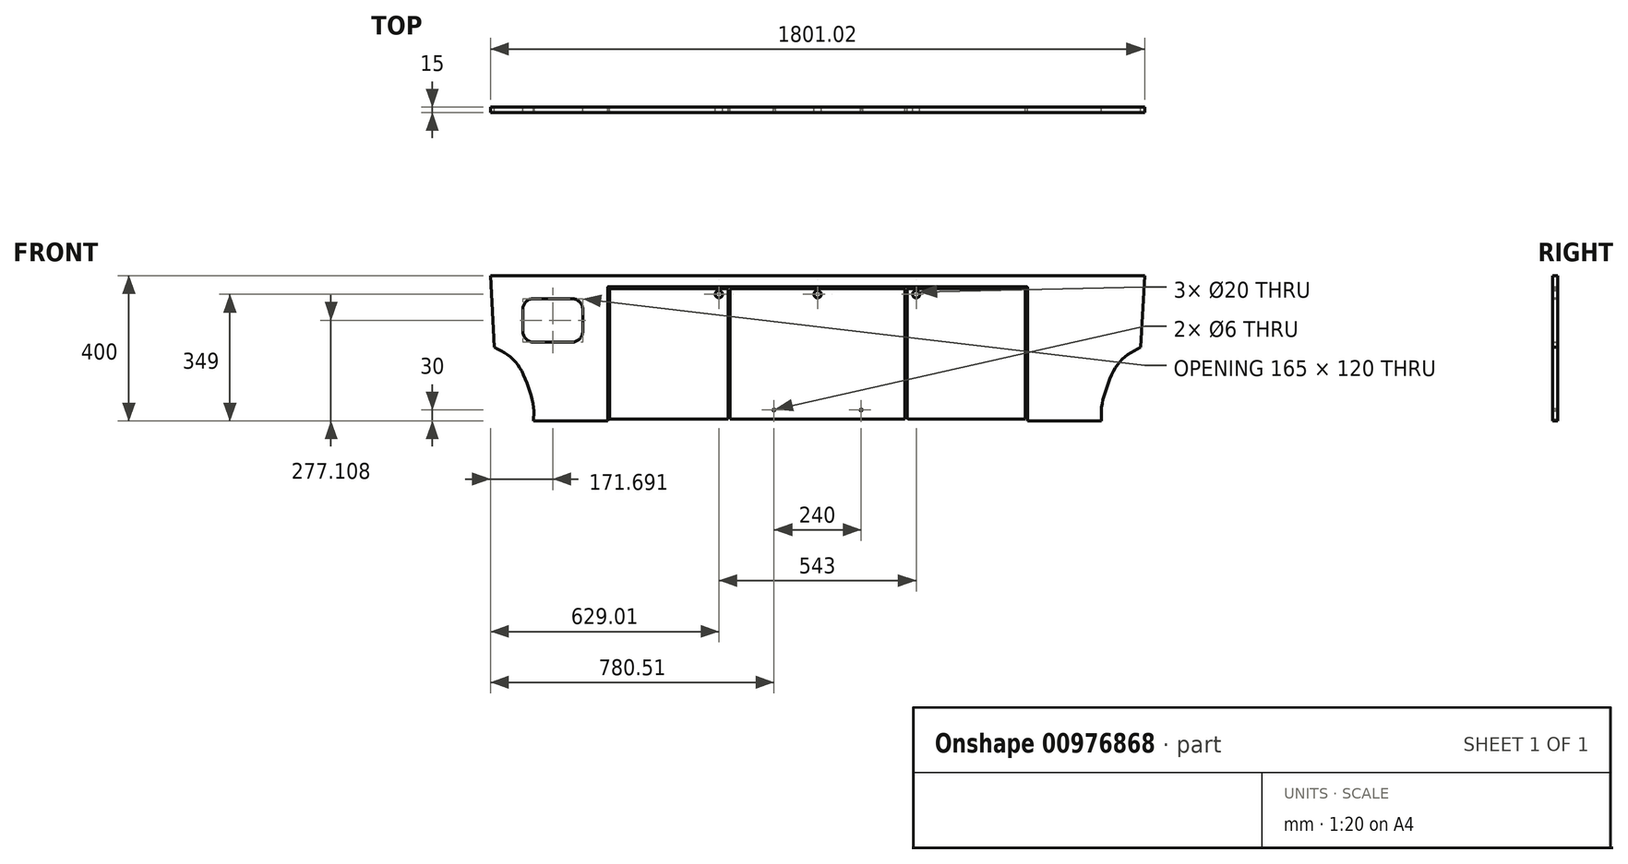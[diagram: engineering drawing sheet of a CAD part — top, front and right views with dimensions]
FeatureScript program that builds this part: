
annotation { "Feature Type Name" : "Feature", "Feature Type Description" : "" }
export const myFeature = defineFeature(function(context is Context, id is Id, definition is map)
    precondition{}
    {
        {
            var Q0;
            Q0=qCreatedBy(makeId("Front.planeOp"),FACE);
            var sketch = newSketch(context, id + "F0", { "sketchPlane" : qUnion([Q0])});
            skLineSegment(sketch, "E0", {"start": v(0, 0) * mm, "end": v(3, 0) * mm});
            skLineSegment(sketch, "E1", {"start": v(575, 0) * mm, "end": v(575, 400) * mm, "construction": true});
            skLineSegment(sketch, "E2", {"start": v(1150, 0) * mm, "end": v(1150, 367) * mm, "construction": true});
            skPoint(sketch, "E3", {"position": v(1357, 0) * mm});
            skLineSegment(sketch, "E4", {"start": v(1153, 0) * mm, "end": v(1357, 0) * mm});
            skPoint(sketch, "E5", {"position": v(1357, 38.33) * mm});
            skPoint(sketch, "E6", {"position": v(1371.58, 94.24) * mm});
            skPoint(sketch, "E7", {"position": v(1395.53, 147.48) * mm});
            skPoint(sketch, "E8", {"position": v(1424.82, 179.42) * mm});
            skPoint(sketch, "E9", {"position": v(1464.75, 203.38) * mm});
            skLineSegment(sketch, "E10.MirrorCS", {"start": v(0, 0) * mm, "end": v(-207, 0) * mm});
            skFitSpline(sketch, "E11", {"points": [v(1357, 0) * mm, v(1357, 38.33) * mm, v(1371.58, 94.24) * mm, v(1395.53, 147.48) * mm, v(1424.82, 179.42) * mm, v(1464.75, 203.38) * mm], "startDerivative": vector(-14.06, 206.16) * mm, "endDerivative": vector(214.46, 114.18) * mm});
            skLineSegment(sketch, "E12", {"start": v(575, 400) * mm, "end": v(1475.51, 400) * mm});
            skLineSegment(sketch, "E13", {"start": v(1475.51, 400) * mm, "end": v(1464.75, 203.38) * mm});
            skLineSegment(sketch, "E14.MirrorCS", {"start": v(575, 400) * mm, "end": v(-325.51, 400) * mm});
            skLineSegment(sketch, "E15.MirrorCS", {"start": v(-325.51, 400) * mm, "end": v(-314.75, 203.38) * mm});
            skFitSpline(sketch, "E16.MirrorCS", {"points": [v(-207, 0) * mm, v(-207, 38.33) * mm, v(-221.58, 94.24) * mm, v(-245.53, 147.48) * mm, v(-274.82, 179.42) * mm, v(-314.75, 203.38) * mm], "startDerivative": vector(14.06, 206.16) * mm, "endDerivative": vector(-214.46, 114.18) * mm});
            skLineSegment(sketch, "E17", {"start": v(0, 367) * mm, "end": v(1150, 367) * mm, "construction": true});
            skLineSegment(sketch, "E18", {"start": v(0, 367) * mm, "end": v(0, 0) * mm, "construction": true});
            skArc(sketch, "E19.0.startCap", {"start": v(-3, 367) * mm, "mid": v(-2.12, 369.12) * mm, "end": v(0, 370) * mm});
            skArc(sketch, "E19.0.endCap", {"start": v(1150, 370) * mm, "mid": v(1152.12, 369.12) * mm, "end": v(1153, 367) * mm});
            skLineSegment(sketch, "E19.0.left", {"start": v(0, 370) * mm, "end": v(1150, 370) * mm});
            skLineSegment(sketch, "E19.0.right", {"start": v(3, 364) * mm, "end": v(323.5, 364) * mm});
            skLineSegment(sketch, "E20.0.left", {"start": v(3, 364) * mm, "end": v(3, 5) * mm});
            skLineSegment(sketch, "E20.0.right", {"start": v(-3, 367) * mm, "end": v(-3, 0) * mm});
            skLineSegment(sketch, "E21.MirrorCS", {"start": v(331.5, 0) * mm, "end": v(331.5, 367) * mm, "construction": true});
            skLineSegment(sketch, "E22.0.left", {"start": v(328.5, 5) * mm, "end": v(328.5, 359) * mm});
            skLineSegment(sketch, "E22.0.right", {"start": v(334.5, 5) * mm, "end": v(334.5, 359) * mm});
            skLineSegment(sketch, "E23.trimOffspring", {"start": v(339.5, 364) * mm, "end": v(810.5, 364) * mm});
            skLineSegment(sketch, "E24.MirrorCS", {"start": v(821.5, 5) * mm, "end": v(821.5, 364) * mm});
            skLineSegment(sketch, "E25.MirrorCS", {"start": v(1147, 364) * mm, "end": v(821.5, 364) * mm});
            skLineSegment(sketch, "E26.MirrorCS", {"start": v(1147, 364) * mm, "end": v(1147, 5) * mm});
            skLineSegment(sketch, "E27.MirrorCS", {"start": v(818.5, 0) * mm, "end": v(818.5, 367) * mm, "construction": true});
            skLineSegment(sketch, "E28.MirrorCS", {"start": v(815.5, 5) * mm, "end": v(815.5, 359) * mm});
            skLineSegment(sketch, "E29.MirrorCS", {"start": v(1153, 367) * mm, "end": v(1153, 0) * mm});
            skLineSegment(sketch, "E30.trimOffspring", {"start": v(821.5, 364) * mm, "end": v(1147, 364) * mm});
            skPoint(sketch, "E20.1.startCap.center.orphan", {"position": v(818.5, 0) * mm});
            skLineSegment(sketch, "E31.bottom", {"start": v(-101.32, 337.1) * mm, "end": v(-206.32, 337.1) * mm});
            skLineSegment(sketch, "E31.top", {"start": v(-101.32, 217.1) * mm, "end": v(-206.32, 217.1) * mm});
            skLineSegment(sketch, "E31.left", {"start": v(-71.32, 307.1) * mm, "end": v(-71.32, 247.1) * mm});
            skLineSegment(sketch, "E31.right", {"start": v(-236.32, 307.1) * mm, "end": v(-236.32, 247.1) * mm});
            skPoint(sketch, "E31.middle", {"position": v(-153.82, 277.1) * mm});
            skPoint(sketch, "E32.visualSharp", {"position": v(-71.32, 337.1) * mm});
            skArc(sketch, "E32.filletArc", {"start": v(-71.32, 307.1) * mm, "mid": v(-80.1, 328.32) * mm, "end": v(-101.32, 337.1) * mm});
            skPoint(sketch, "E33.visualSharp", {"position": v(-236.32, 337.1) * mm});
            skArc(sketch, "E33.filletArc", {"start": v(-206.32, 337.1) * mm, "mid": v(-227.53, 328.32) * mm, "end": v(-236.32, 307.1) * mm});
            skPoint(sketch, "E34.visualSharp", {"position": v(-71.32, 217.1) * mm});
            skArc(sketch, "E34.filletArc", {"start": v(-101.32, 217.1) * mm, "mid": v(-80.1, 225.9) * mm, "end": v(-71.32, 247.1) * mm});
            skPoint(sketch, "E35.visualSharp", {"position": v(-236.32, 217.1) * mm});
            skArc(sketch, "E35.filletArc", {"start": v(-236.32, 247.1) * mm, "mid": v(-227.53, 225.9) * mm, "end": v(-206.32, 217.1) * mm});
            skPoint(sketch, "E36.MirrorP", {"position": v(392.64, 490.65) * mm});
            skPoint(sketch, "E37", {"position": v(1147, 5) * mm});
            skPoint(sketch, "E38.MirrorP", {"position": v(3, 5) * mm});
            skLineSegment(sketch, "E39", {"start": v(1147, 5) * mm, "end": v(3, 5) * mm});
            skPoint(sketch, "E40.orphan", {"position": v(3, 0) * mm});
            skPoint(sketch, "E41.orphan", {"position": v(334.5, 0) * mm});
            skPoint(sketch, "E42.orphan", {"position": v(328.5, 0) * mm});
            skPoint(sketch, "E43.orphan", {"position": v(815.5, 0) * mm});
            skPoint(sketch, "E44.orphan", {"position": v(821.5, 0) * mm});
            skPoint(sketch, "E45.trimOffspring.start.orphan", {"position": v(1147, 0) * mm});
            skPoint(sketch, "E46.visualSharp", {"position": v(328.5, 364) * mm});
            skArc(sketch, "E46.filletArc", {"start": v(328.5, 359) * mm, "mid": v(327.04, 362.54) * mm, "end": v(323.5, 364) * mm});
            skPoint(sketch, "E47.visualSharp", {"position": v(334.5, 364) * mm});
            skArc(sketch, "E47.filletArc", {"start": v(339.5, 364) * mm, "mid": v(335.96, 362.54) * mm, "end": v(334.5, 359) * mm});
            skPoint(sketch, "E48.visualSharp", {"position": v(815.5, 364) * mm});
            skArc(sketch, "E48.filletArc", {"start": v(815.5, 359) * mm, "mid": v(814.04, 362.54) * mm, "end": v(810.5, 364) * mm});
            skSolve(sketch);
        }
        {
            var Q0;
            {var subQ3=sQuery(id+"F0.wireOp",EDGE,"E20.0.endCap");Q0=makeQuery(id+"F0.imprint","IMPRINT",FACE,{"disambiguationData":[TD([[makeQuery(id+"F0.imprint","IMPRINT",EDGE,{"derivedFrom":subQ3}),-1.0]])]});}
            var Q1;
            {var subQ0=sQuery(id+"F0.wireOp",EDGE,"E20.1.startCap");Q1=makeQuery(id+"F0.imprint","IMPRINT",FACE,{"disambiguationData":[TD([[makeQuery(id+"F0.imprint","IMPRINT",EDGE,{"derivedFrom":subQ0}),-1.0]])]});}
            var Q2;
            {var subQ0=sQuery(id+"F0.wireOp",EDGE,"E20.0.left");var subQ5=sQuery(id+"F0.wireOp",EDGE,"E19.0.right");var subQ6=makeQuery(id+"F0.imprint","INTERSECT",VERTEX,{"derivedFrom":[subQ5,subQ0]});Q2=makeQuery(id+"F0.imprint","IMPRINT",FACE,{"disambiguationData":[TD([[makeQuery(id+"F0.imprint","IMPRINT",EDGE,{"disambiguationData":[TD([[subQ6,-1.0]])],"derivedFrom":subQ5}),-1.0]])]});}
            var Q3;
            {var subQ1=sQuery(id+"F0.wireOp",EDGE,"E19.0.startCap");Q3=makeQuery(id+"F0.imprint","IMPRINT",FACE,{"disambiguationData":[TD([[makeQuery(id+"F0.imprint","IMPRINT",EDGE,{"derivedFrom":subQ1}),1.0]])]});}
            var Q4;
            {var subQ4=sQuery(id+"F0.wireOp",EDGE,"E20.1.left");var subQ6=sQuery(id+"F0.wireOp",EDGE,"E19.0.right");var subQ7=makeQuery(id+"F0.imprint","INTERSECT",VERTEX,{"derivedFrom":[subQ6,subQ4]});Q4=makeQuery(id+"F0.imprint","IMPRINT",FACE,{"disambiguationData":[TD([[makeQuery(id+"F0.imprint","IMPRINT",EDGE,{"disambiguationData":[TD([[subQ7,-1.0]])],"derivedFrom":subQ6}),-1.0]])]});}
            var Q5;
            {var subQ0=sQuery(id+"F0.wireOp",EDGE,"E26.MirrorCS");Q5=makeQuery(id+"F0.imprint","IMPRINT",FACE,{"disambiguationData":[TD([[makeQuery(id+"F0.imprint","IMPRINT",EDGE,{"derivedFrom":subQ0}),-1.0]])]});}
            var Q6;
            {var subQ1=sQuery(id+"F0.wireOp",EDGE,"E11");Q6=makeQuery(id+"F0.imprint","IMPRINT",FACE,{"disambiguationData":[TD([[makeQuery(id+"F0.imprint","IMPRINT",EDGE,{"derivedFrom":subQ1}),1.0]])]});}
            var Q7;
            {var subQ2=sQuery(id+"F0.wireOp",EDGE,"E22.0.right");Q7=makeQuery(id+"F0.imprint","IMPRINT",FACE,{"disambiguationData":[TD([[makeQuery(id+"F0.imprint","IMPRINT",EDGE,{"derivedFrom":subQ2}),-1.0]])]});}
            extrude(context, id + "F1", {"entities" : qUnion([Q0, Q1, Q2, Q3, Q4, Q5, Q6, Q7]), "depth" : 15 * mm, "offsetDistance" : 25 * mm});
        }
        {
            var Q0;
            Q0=qCreatedBy(makeId("Front.planeOp"),FACE);
            var sketch = newSketch(context, id + "F2", { "sketchPlane" : qUnion([Q0])});
            skPoint(sketch, "E49", {"position": v(846.5, 349) * mm});
            skPoint(sketch, "E50.MirrorP", {"position": v(303.5, 349) * mm});
            skPoint(sketch, "E51", {"position": v(575.16, 349) * mm});
            skLineSegment(sketch, "E52", {"start": v(-147.55, 387.12) * mm, "end": v(-147.55, 102.02) * mm, "construction": true});
            skSolve(sketch);
        }
        {
            var Q0;
            Q0=sQuery(id+"F2.wireOp",VERTEX,"E49");
            var Q1;
            Q1=sQuery(id+"F2.wireOp",VERTEX,"E50.MirrorP");
            var Q2;
            Q2=makeQuery(id+"F1.opExtrude","SWEPT_BODY",BODY,{"disambiguationData":[OSD([sQuery(id+"F0.wireOp",EDGE,"E26.MirrorCS"),sQuery(id+"F0.wireOp",EDGE,"E24.MirrorCS"),sQuery(id+"F0.wireOp",EDGE,"E30.trimOffspring"),sQuery(id+"F0.wireOp",EDGE,"E45.trimOffspring")])]});
            var Q3;
            Q3=makeQuery(id+"F1.opExtrude","SWEPT_BODY",BODY,{"disambiguationData":[OSD([sQuery(id+"F0.wireOp",EDGE,"E0"),sQuery(id+"F0.wireOp",EDGE,"E19.0.right"),sQuery(id+"F0.wireOp",EDGE,"E20.0.left"),sQuery(id+"F0.wireOp",EDGE,"E22.0.left")])]});
            hole(context, id + "F3", {"style" : HoleStyle.SIMPLE, "endStyle" : HoleEndStyle.THROUGH, "oppositeDirection" : true, "holeDiameter" : 20 * mm, "majorDiameter" : 5 * mm, "isTappedThrough" : true, "tappedDepth" : 12 * mm, "tapClearance" : 3, "locations" : qUnion([Q0, Q1]), "scope" : qUnion([Q2, Q3])});
        }
        {
            var Q0;
            Q0=sQuery(id+"F2.wireOp",VERTEX,"E51");
            var Q1;
            Q1=makeQuery(id+"F1.opExtrude","SWEPT_BODY",BODY,{"disambiguationData":[OSD([sQuery(id+"F0.wireOp",EDGE,"E0"),sQuery(id+"F0.wireOp",EDGE,"E22.0.right"),sQuery(id+"F0.wireOp",EDGE,"E23.trimOffspring"),sQuery(id+"F0.wireOp",EDGE,"E28.MirrorCS")])]});
            hole(context, id + "F4", {"style" : HoleStyle.SIMPLE, "endStyle" : HoleEndStyle.THROUGH, "oppositeDirection" : true, "holeDiameter" : 20 * mm, "majorDiameter" : 5 * mm, "isTappedThrough" : true, "tappedDepth" : 12 * mm, "tapClearance" : 3, "locations" : qUnion([Q0]), "scope" : qUnion([Q1])});
        }
        {
            var Q0;
            Q0=makeQuery(id+"F1.opExtrude","CAP_FACE",FACE,{"disambiguationData":[OSD([sQuery(id+"F0.wireOp",EDGE,"E22.0.right"),sQuery(id+"F0.wireOp",EDGE,"E23.trimOffspring"),sQuery(id+"F0.wireOp",EDGE,"E28.MirrorCS"),sQuery(id+"F0.wireOp",EDGE,"E39")])],"isStart":false});
            var sketch = newSketch(context, id + "F5", { "sketchPlane" : qUnion([Q0])});
            skPoint(sketch, "E53", {"position": v(455, 30) * mm});
            skPoint(sketch, "E54.MirrorP", {"position": v(695, 30) * mm});
            skSolve(sketch);
        }
        {
            var Q0;
            Q0=sQuery(id+"F5.wireOp",VERTEX,"E53");
            var Q1;
            Q1=sQuery(id+"F5.wireOp",VERTEX,"E54.MirrorP");
            var Q2;
            Q2=makeQuery(id+"F1.opExtrude","SWEPT_BODY",BODY,{"disambiguationData":[OSD([sQuery(id+"F0.wireOp",EDGE,"E22.0.right"),sQuery(id+"F0.wireOp",EDGE,"E23.trimOffspring"),sQuery(id+"F0.wireOp",EDGE,"E28.MirrorCS"),sQuery(id+"F0.wireOp",EDGE,"E39")])]});
            hole(context, id + "F6", {"style" : HoleStyle.SIMPLE, "endStyle" : HoleEndStyle.BLIND, "holeDiameter" : 6 * mm, "majorDiameter" : 5 * mm, "holeDepth" : 10 * mm, "isTappedThrough" : true, "tappedDepth" : 12 * mm, "tapClearance" : 3, "startFromSketch" : true, "locations" : qUnion([Q0, Q1]), "scope" : qUnion([Q2])});
        }
        {
            var Q0;
            Q0=makeQuery(id+"F1.opExtrude","SWEPT_EDGE",EDGE,{"disambiguationData":[OSD([sQuery(id+"F0.wireOp",EDGE,"E24.MirrorCS"),sQuery(id+"F0.wireOp",EDGE,"E30.trimOffspring")])]});
            fillet(context, id + "F7", {"entities" : qUnion([Q0]), "radius" : 5 * mm, "tangentPropagation" : true, "allowEdgeOverflow" : false});
        }
    });
